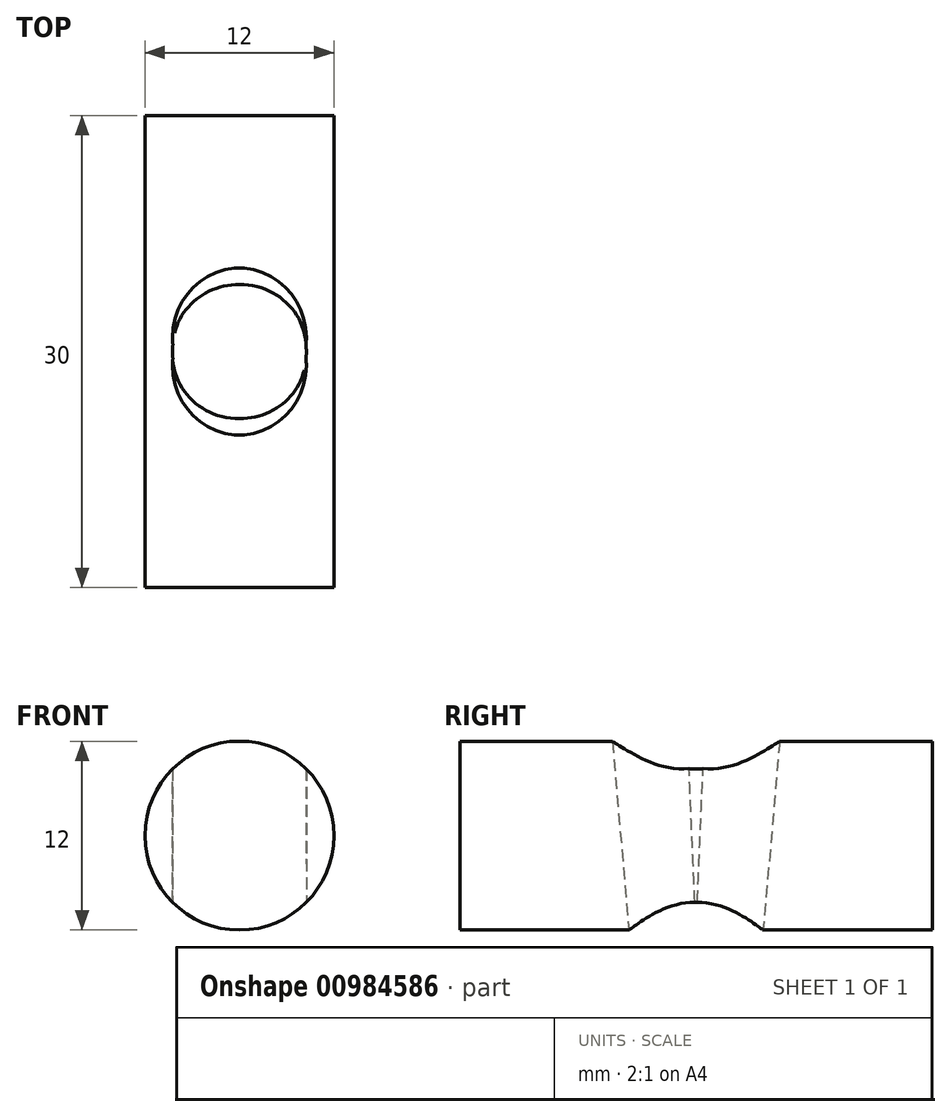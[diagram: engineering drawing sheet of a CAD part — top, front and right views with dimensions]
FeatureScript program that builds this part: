
annotation { "Feature Type Name" : "Feature", "Feature Type Description" : "" }
export const myFeature = defineFeature(function(context is Context, id is Id, definition is map)
    precondition{}
    {
        {
            var Q0;
            Q0=qCreatedBy(makeId("Front.planeOp"),FACE);
            var sketch = newSketch(context, id + "F0", { "sketchPlane" : qUnion([Q0])});
            skCircle(sketch, "E0", {"center": v(0, 0) * mm, "radius": 6 * mm});
            skSolve(sketch);
        }
        {
            var Q0;
            Q0=makeQuery(id+"F0.imprint","IMPRINT",FACE,{"disambiguationData":[TD([[makeQuery(id+"F0.imprint","IMPRINT",EDGE,{"derivedFrom":sQuery(id+"F0.wireOp",EDGE,"E0")}),1.0]])]});
            extrude(context, id + "F1", {"entities" : qUnion([Q0]), "depth" : 30 * mm, "offsetDistance" : 25 * mm});
        }
        {
            var Q0;
            Q0=qCreatedBy(makeId("Top.planeOp"),FACE);
            cPlane(context, id + "F2", {"entities" : qUnion([Q0]), "cplaneType" : CPlaneType.OFFSET, "offset" : 6 * mm, "oppositeDirection" : true, "width" : 150 * mm, "height" : 150 * mm});
        }
        {
            var Q0;
            Q0=qCreatedBy(id+"F2.planeOp",FACE);
            var sketch = newSketch(context, id + "F3", { "sketchPlane" : qUnion([Q0])});
            skCircle(sketch, "E1", {"center": v(0, -15) * mm, "radius": 4.25 * mm});
            skLineSegment(sketch, "E2", {"start": v(0, -15) * mm, "end": v(45.13, -15) * mm});
            skSolve(sketch);
        }
        {
            var Q0;
            Q0=qCreatedBy(id+"F2.planeOp",FACE);
            var Q1;
            Q1=sQuery(id+"F3.wireOp",EDGE,"E2");
            cPlane(context, id + "F4", {"entities" : qUnion([Q0, Q1]), "cplaneType" : CPlaneType.LINE_ANGLE, "offset" : 25 * mm, "angle" : 5 * degree, "width" : 150 * mm, "height" : 150 * mm});
        }
        {
            var Q0;
            Q0=qCreatedBy(id+"F2.planeOp",FACE);
            var Q1;
            Q1=sQuery(id+"F3.wireOp",EDGE,"E2");
            cPlane(context, id + "F5", {"entities" : qUnion([Q0, Q1]), "cplaneType" : CPlaneType.LINE_ANGLE, "offset" : 25 * mm, "angle" : 5 * degree, "oppositeDirection" : true, "width" : 150 * mm, "height" : 150 * mm});
        }
        {
            var Q0;
            Q0=qCreatedBy(id+"F4.planeOp",FACE);
            var sketch = newSketch(context, id + "F6", { "sketchPlane" : qUnion([Q0])});
            skCircle(sketch, "E3", {"center": v(0, 15.47) * mm, "radius": 4.25 * mm});
            skSolve(sketch);
        }
        {
            var Q0;
            Q0=qCreatedBy(id+"F5.planeOp",FACE);
            var sketch = newSketch(context, id + "F7", { "sketchPlane" : qUnion([Q0])});
            skCircle(sketch, "E4", {"center": v(0, 14.42) * mm, "radius": 4.25 * mm});
            skSolve(sketch);
        }
        {
            var Q0;
            Q0 = qSketchRegion(id + "F6", true);
            extrude(context, id + "F8", {"entities" : qUnion([Q0]), "operationType" : NewBodyOperationType.REMOVE, "endBound" : BoundingType.THROUGH_ALL, "oppositeDirection" : true, "depth" : 25 * mm, "offsetDistance" : 25 * mm});
        }
        {
            var Q0;
            Q0 = qSketchRegion(id + "F7", true);
            extrude(context, id + "F9", {"entities" : qUnion([Q0]), "operationType" : NewBodyOperationType.REMOVE, "endBound" : BoundingType.THROUGH_ALL, "oppositeDirection" : true, "depth" : 25 * mm, "offsetDistance" : 25 * mm});
        }
        {
            var Q0;
            Q0 = qSketchRegion(id + "F3", true);
            extrude(context, id + "F10", {"entities" : qUnion([Q0]), "operationType" : NewBodyOperationType.REMOVE, "endBound" : BoundingType.THROUGH_ALL, "depth" : 25 * mm, "offsetDistance" : 25 * mm});
        }
    });
